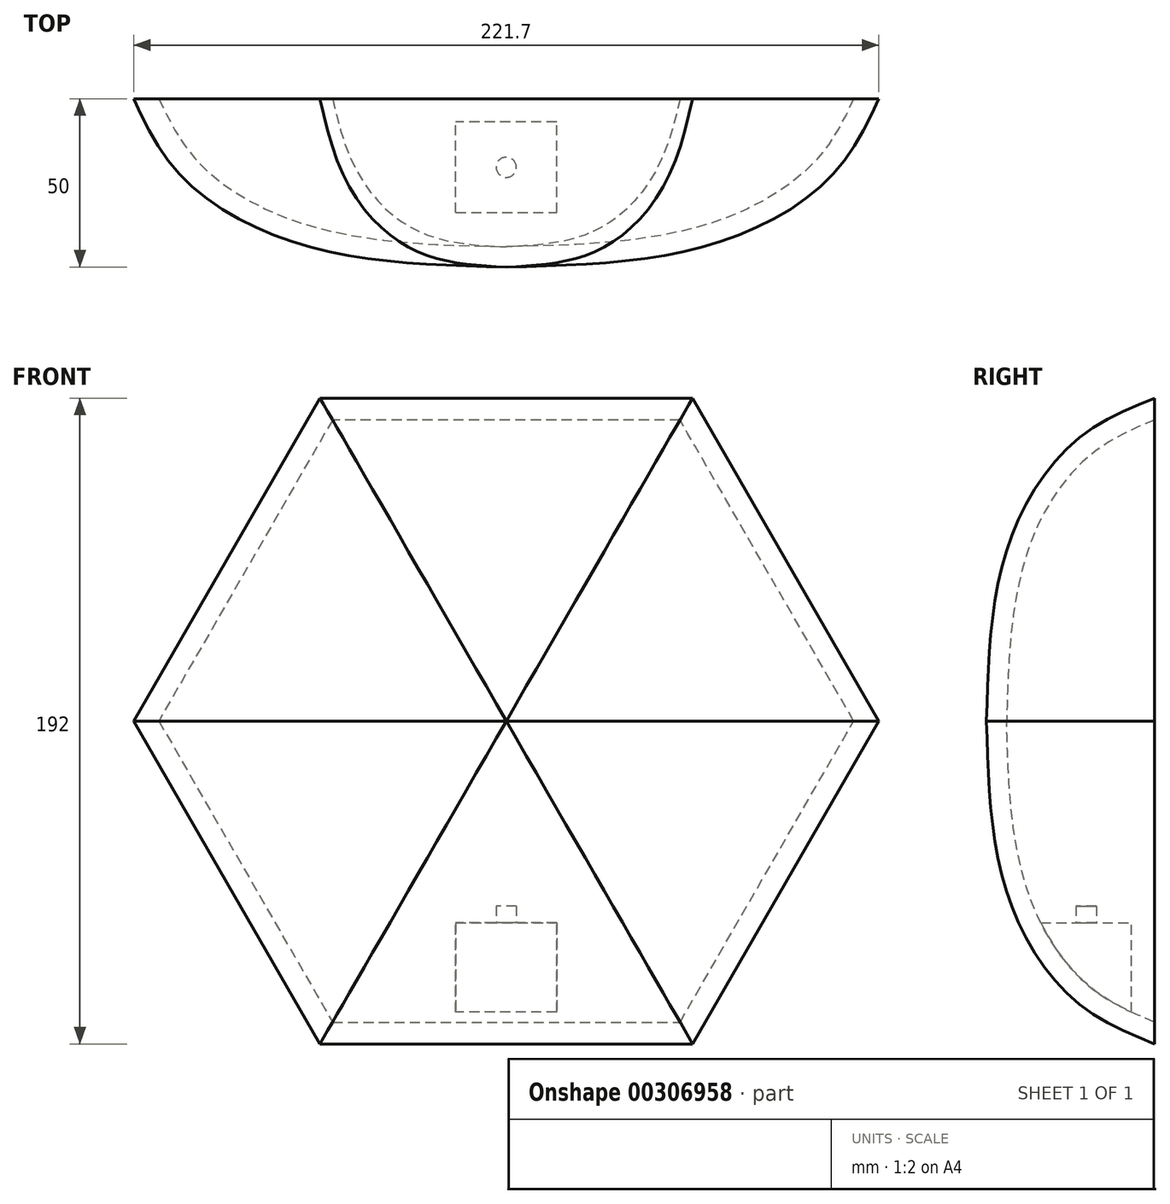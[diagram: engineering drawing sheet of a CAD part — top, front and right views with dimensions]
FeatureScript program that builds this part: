
annotation { "Feature Type Name" : "Feature", "Feature Type Description" : "" }
export const myFeature = defineFeature(function(context is Context, id is Id, definition is map)
    precondition{}
    {
        {
            var Q0;
            Q0=qCreatedBy(makeId("Front.planeOp"),FACE);
            var sketch = newSketch(context, id + "F0", { "sketchPlane" : qUnion([Q0])});
            skCircle(sketch, "E0.cCircle", {"center": v(0, 0) * mm, "radius": 96 * mm, "construction": true});
            skLineSegment(sketch, "E0.0", {"start": v(-55.43, 96) * mm, "end": v(55.43, 96) * mm});
            skLineSegment(sketch, "E0.1", {"start": v(55.43, 96) * mm, "end": v(110.85, 0) * mm});
            skLineSegment(sketch, "E0.2", {"start": v(110.85, 0) * mm, "end": v(55.43, -96) * mm});
            skLineSegment(sketch, "E0.3", {"start": v(55.43, -96) * mm, "end": v(-55.43, -96) * mm});
            skLineSegment(sketch, "E0.4", {"start": v(-55.43, -96) * mm, "end": v(-110.85, 0) * mm});
            skLineSegment(sketch, "E0.5", {"start": v(-110.85, 0) * mm, "end": v(-55.43, 96) * mm});
            skPoint(sketch, "E0.0.midPoint", {"position": v(0, 96) * mm});
            skSolve(sketch);
        }
        {
            var Q0;
            Q0=qCreatedBy(makeId("Front.planeOp"),FACE);
            cPlane(context, id + "F1", {"entities" : qUnion([Q0]), "cplaneType" : CPlaneType.OFFSET, "offset" : 20 * mm, "width" : 150 * mm, "height" : 150 * mm});
        }
        {
            var Q0;
            Q0=qCreatedBy(id+"F1.planeOp",FACE);
            var sketch = newSketch(context, id + "F2", { "sketchPlane" : qUnion([Q0])});
            skCircle(sketch, "E1.cCircle", {"center": v(0, 0) * mm, "radius": 86 * mm, "construction": true});
            skLineSegment(sketch, "E1.0", {"start": v(-49.65, 86) * mm, "end": v(49.65, 86) * mm});
            skLineSegment(sketch, "E1.1", {"start": v(49.65, 86) * mm, "end": v(99.3, 0) * mm});
            skLineSegment(sketch, "E1.2", {"start": v(99.3, 0) * mm, "end": v(49.65, -86) * mm});
            skLineSegment(sketch, "E1.3", {"start": v(49.65, -86) * mm, "end": v(-49.65, -86) * mm});
            skLineSegment(sketch, "E1.4", {"start": v(-49.65, -86) * mm, "end": v(-99.3, 0) * mm});
            skLineSegment(sketch, "E1.5", {"start": v(-99.3, 0) * mm, "end": v(-49.65, 86) * mm});
            skPoint(sketch, "E1.0.midPoint", {"position": v(0, 86) * mm});
            skSolve(sketch);
        }
        {
            var Q0;
            Q0=qCreatedBy(id+"F1.planeOp",FACE);
            cPlane(context, id + "F3", {"entities" : qUnion([Q0]), "cplaneType" : CPlaneType.OFFSET, "offset" : 20 * mm, "width" : 150 * mm, "height" : 150 * mm});
        }
        {
            var Q0;
            Q0=qCreatedBy(id+"F3.planeOp",FACE);
            var sketch = newSketch(context, id + "F4", { "sketchPlane" : qUnion([Q0])});
            skCircle(sketch, "E2.cCircle", {"center": v(0, 0) * mm, "radius": 61 * mm, "construction": true});
            skLineSegment(sketch, "E2.0", {"start": v(-35.22, 61) * mm, "end": v(35.22, 61) * mm});
            skLineSegment(sketch, "E2.1", {"start": v(35.22, 61) * mm, "end": v(70.44, 0) * mm});
            skLineSegment(sketch, "E2.2", {"start": v(70.44, 0) * mm, "end": v(35.22, -61) * mm});
            skLineSegment(sketch, "E2.3", {"start": v(35.22, -61) * mm, "end": v(-35.22, -61) * mm});
            skLineSegment(sketch, "E2.4", {"start": v(-35.22, -61) * mm, "end": v(-70.44, 0) * mm});
            skLineSegment(sketch, "E2.5", {"start": v(-70.44, 0) * mm, "end": v(-35.22, 61) * mm});
            skPoint(sketch, "E2.0.midPoint", {"position": v(0, 61) * mm});
            skSolve(sketch);
        }
        {
            var Q0;
            Q0=qCreatedBy(id+"F3.planeOp",FACE);
            cPlane(context, id + "F5", {"entities" : qUnion([Q0]), "cplaneType" : CPlaneType.OFFSET, "offset" : 10 * mm, "width" : 150 * mm, "height" : 150 * mm});
        }
        {
            var Q0;
            Q0=qCreatedBy(id+"F5.planeOp",FACE);
            var sketch = newSketch(context, id + "F6", { "sketchPlane" : qUnion([Q0])});
            skPoint(sketch, "E3", {"position": v(0, 0) * mm});
            skSolve(sketch);
        }
        {
            var Q0;
            Q0=makeQuery(id+"F0.imprint","IMPRINT",FACE,{"disambiguationData":[TD([[makeQuery(id+"F0.imprint","IMPRINT",EDGE,{"derivedFrom":sQuery(id+"F0.wireOp",EDGE,"E0.0")}),-1.0]])]});
            var Q1;
            Q1=makeQuery(id+"F2.imprint","IMPRINT",FACE,{"disambiguationData":[TD([[makeQuery(id+"F2.imprint","IMPRINT",EDGE,{"derivedFrom":sQuery(id+"F2.wireOp",EDGE,"E1.0")}),-1.0]])]});
            var Q2;
            Q2=makeQuery(id+"F4.imprint","IMPRINT",FACE,{"disambiguationData":[TD([[makeQuery(id+"F4.imprint","IMPRINT",EDGE,{"derivedFrom":sQuery(id+"F4.wireOp",EDGE,"E2.0")}),-1.0]])]});
            var Q3;
            Q3=sQuery(id+"F6.wireOp",VERTEX,"E3");
            loft(context, id + "F7", {"sheetProfilesArray" : [{ "sheetProfileEntities" : qUnion([Q0]) }, { "sheetProfileEntities" : qUnion([Q1]) }, { "sheetProfileEntities" : qUnion([Q2]) }, { "sheetProfileEntities" : qUnion([Q3]) }]});
        }
        {
            var Q0;
            Q0=makeQuery(id+"F7.opLoft","CAP_FACE",FACE,{"disambiguationData":[OSD([makeQuery(id+"F0.imprint","IMPRINT",FACE,{"disambiguationData":[TD([[makeQuery(id+"F0.imprint","IMPRINT",EDGE,{"derivedFrom":sQuery(id+"F0.wireOp",EDGE,"E0.0")}),-1.0]])]})])],"isStart":true});
            shell(context, id + "F8", {"entities" : qUnion([Q0]), "thickness" : 6 * mm});
        }
        {
            var Q0;
            Q0=qCreatedBy(makeId("Top.planeOp"),FACE);
            cPlane(context, id + "F9", {"entities" : qUnion([Q0]), "cplaneType" : CPlaneType.OFFSET, "offset" : 60 * mm, "oppositeDirection" : true, "width" : 150 * mm, "height" : 150 * mm});
        }
        {
            var Q0;
            Q0=qCreatedBy(id+"F9.planeOp",FACE);
            var sketch = newSketch(context, id + "F10", { "sketchPlane" : qUnion([Q0])});
            skLineSegment(sketch, "E4.bottom", {"start": v(15, -36.85) * mm, "end": v(-15, -36.85) * mm});
            skLineSegment(sketch, "E4.top", {"start": v(15, -6.85) * mm, "end": v(-15, -6.85) * mm});
            skLineSegment(sketch, "E4.left", {"start": v(15, -36.85) * mm, "end": v(15, -6.85) * mm});
            skLineSegment(sketch, "E4.right", {"start": v(-15, -36.85) * mm, "end": v(-15, -6.85) * mm});
            skPoint(sketch, "E4.middle", {"position": v(0, -21.85) * mm});
            skSolve(sketch);
        }
        {
            var Q0;
            Q0 = qSketchRegion(id + "F10", true);
            extrude(context, id + "F11", {"entities" : qUnion([Q0]), "operationType" : NewBodyOperationType.ADD, "endBound" : BoundingType.UP_TO_NEXT, "oppositeDirection" : true, "depth" : 20 * mm});
        }
        {
            var Q0;
            Q0=makeQuery(id+"F11.opExtrude","CAP_FACE",FACE,{"disambiguationData":[OSD([sQuery(id+"F10.wireOp",EDGE,"E4.bottom"),sQuery(id+"F10.wireOp",EDGE,"E4.top"),sQuery(id+"F10.wireOp",EDGE,"E4.left"),sQuery(id+"F10.wireOp",EDGE,"E4.right")])],"isStart":true});
            var sketch = newSketch(context, id + "F12", { "sketchPlane" : qUnion([Q0])});
            skCircle(sketch, "E5", {"center": v(0, -20.34) * mm, "radius": 3 * mm});
            skPoint(sketch, "E5.centerSnap0", {"position": v(15, -20.34) * mm});
            skSolve(sketch);
        }
        {
            var Q0;
            Q0 = qSketchRegion(id + "F12", true);
            extrude(context, id + "F13", {"entities" : qUnion([Q0]), "operationType" : NewBodyOperationType.ADD, "depth" : 5 * mm});
        }
    });
